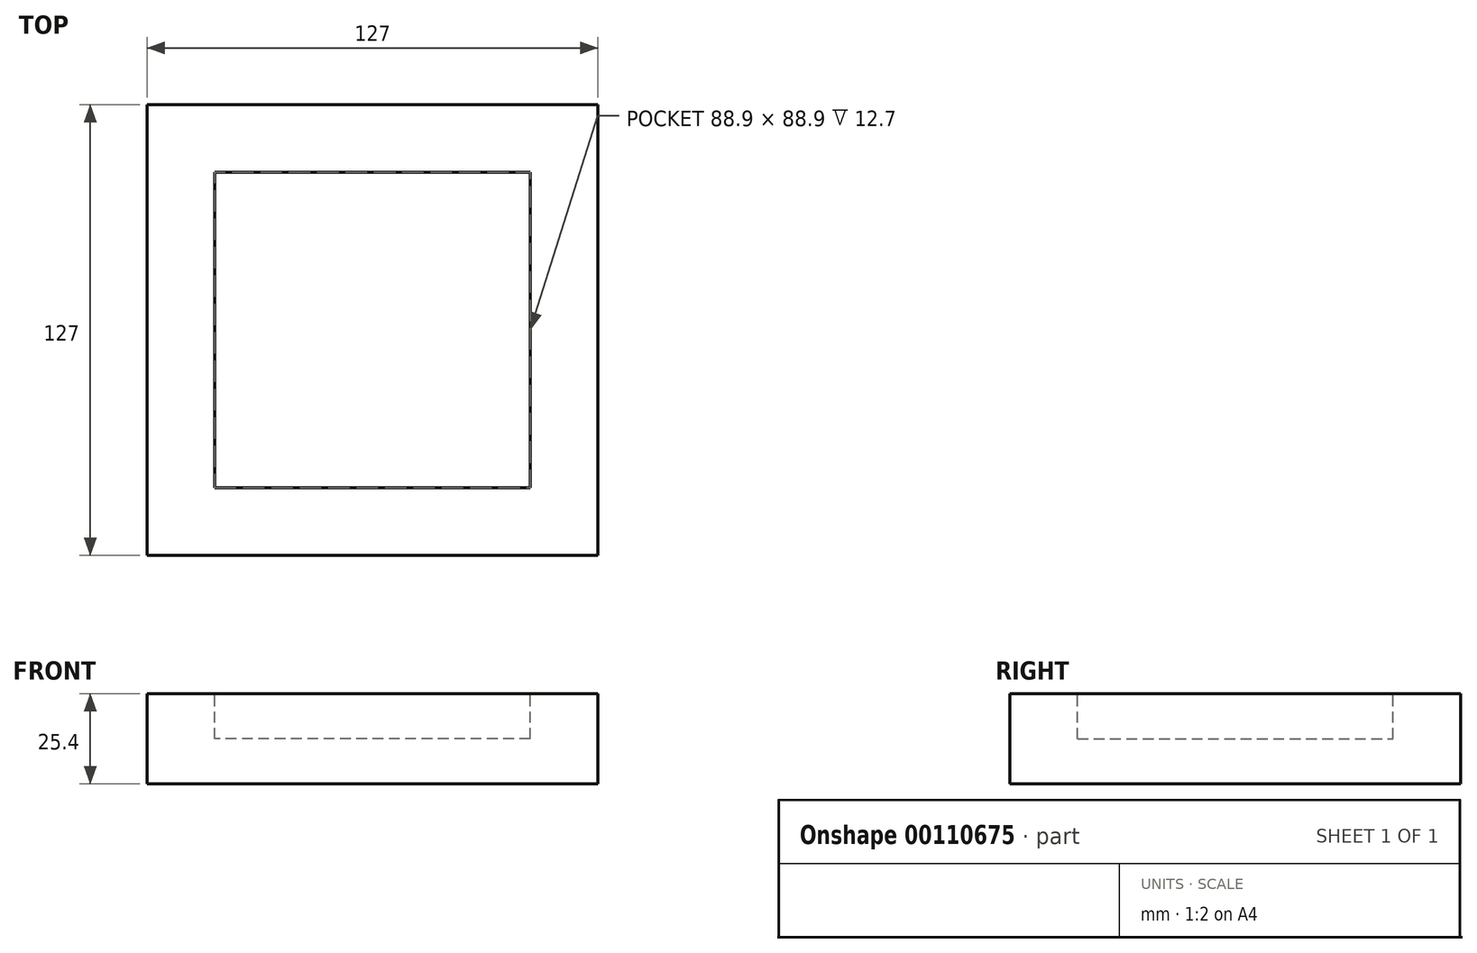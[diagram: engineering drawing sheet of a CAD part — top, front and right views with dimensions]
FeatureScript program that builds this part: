
annotation { "Feature Type Name" : "Feature", "Feature Type Description" : "" }
export const myFeature = defineFeature(function(context is Context, id is Id, definition is map)
    precondition{}
    {
        {
            var Q0;
            Q0=qCreatedBy(makeId("Top.planeOp"),FACE);
            var sketch = newSketch(context, id + "F0", { "sketchPlane" : qUnion([Q0])});
            skLineSegment(sketch, "E0.bottom", {"start": v(-63.5, -63.5) * mm, "end": v(63.5, -63.5) * mm});
            skLineSegment(sketch, "E0.top", {"start": v(-63.5, 63.5) * mm, "end": v(63.5, 63.5) * mm});
            skLineSegment(sketch, "E0.left", {"start": v(-63.5, -63.5) * mm, "end": v(-63.5, 63.5) * mm});
            skLineSegment(sketch, "E0.right", {"start": v(63.5, -63.5) * mm, "end": v(63.5, 63.5) * mm});
            skPoint(sketch, "E0.middle", {"position": v(0, 0) * mm});
            skSolve(sketch);
        }
        {
            var Q0;
            Q0 = qSketchRegion(id + "F0", true);
            extrude(context, id + "F1", {"entities" : qUnion([Q0]), "depth" : 25.4 * mm});
        }
        {
            var Q0;
            Q0=makeQuery(id+"F1.opExtrude","CAP_FACE",FACE,{"disambiguationData":[OSD([sQuery(id+"F0.wireOp",EDGE,"E0.bottom"),sQuery(id+"F0.wireOp",EDGE,"E0.top"),sQuery(id+"F0.wireOp",EDGE,"E0.left"),sQuery(id+"F0.wireOp",EDGE,"E0.right")])],"isStart":false});
            var sketch = newSketch(context, id + "F2", { "sketchPlane" : qUnion([Q0])});
            skLineSegment(sketch, "E1.bottom", {"start": v(44.45, -44.45) * mm, "end": v(-44.45, -44.45) * mm});
            skLineSegment(sketch, "E1.top", {"start": v(44.45, 44.45) * mm, "end": v(-44.45, 44.45) * mm});
            skLineSegment(sketch, "E1.left", {"start": v(44.45, -44.45) * mm, "end": v(44.45, 44.45) * mm});
            skLineSegment(sketch, "E1.right", {"start": v(-44.45, -44.45) * mm, "end": v(-44.45, 44.45) * mm});
            skPoint(sketch, "E1.middle", {"position": v(0, 0) * mm});
            skSolve(sketch);
        }
        {
            var Q0;
            Q0 = qSketchRegion(id + "F2", true);
            extrude(context, id + "F3", {"entities" : qUnion([Q0]), "operationType" : NewBodyOperationType.REMOVE, "oppositeDirection" : true, "depth" : 12.7 * mm});
        }
    });
